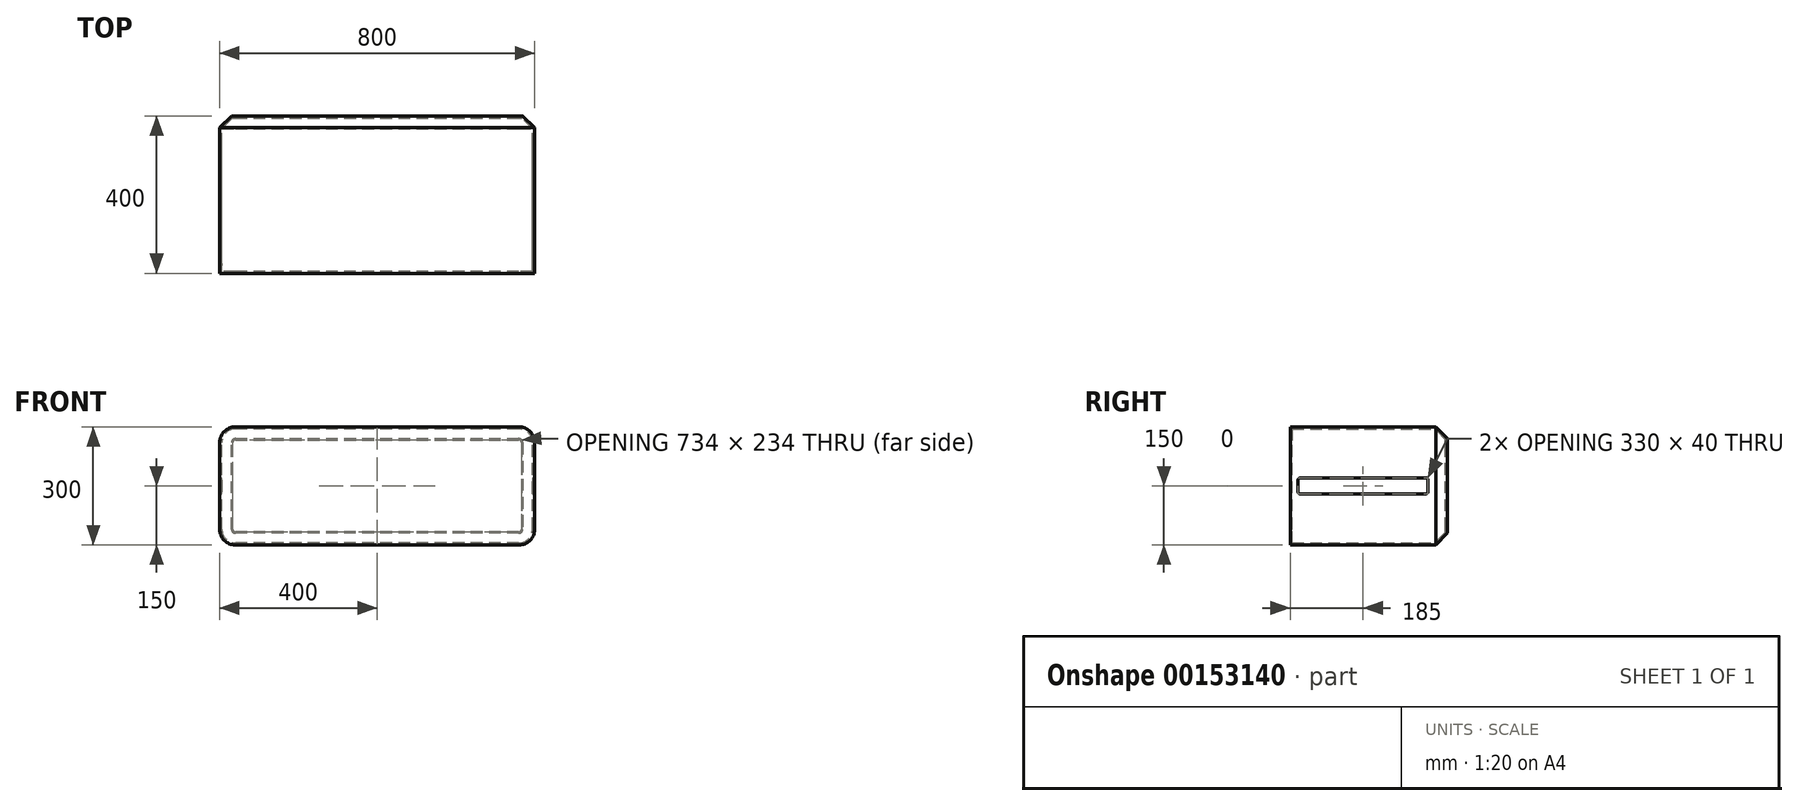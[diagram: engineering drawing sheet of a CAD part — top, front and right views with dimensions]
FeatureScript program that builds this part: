
annotation { "Feature Type Name" : "Feature", "Feature Type Description" : "" }
export const myFeature = defineFeature(function(context is Context, id is Id, definition is map)
    precondition{}
    {
        {
            var Q0;
            Q0=qCreatedBy(makeId("Front.planeOp"),FACE);
            var sketch = newSketch(context, id + "F0", { "sketchPlane" : qUnion([Q0])});
            skLineSegment(sketch, "E0.bottom", {"start": v(400, -150) * mm, "end": v(-400, -150) * mm});
            skLineSegment(sketch, "E0.top", {"start": v(400, 150) * mm, "end": v(-400, 150) * mm});
            skLineSegment(sketch, "E0.left", {"start": v(400, -150) * mm, "end": v(400, 150) * mm});
            skLineSegment(sketch, "E0.right", {"start": v(-400, -150) * mm, "end": v(-400, 150) * mm});
            skPoint(sketch, "E0.middle", {"position": v(0, 0) * mm});
            skSolve(sketch);
        }
        {
            var Q0;
            Q0=makeQuery(id+"F0.imprint","IMPRINT",FACE,{"disambiguationData":[TD([[makeQuery(id+"F0.imprint","IMPRINT",EDGE,{"derivedFrom":sQuery(id+"F0.wireOp",EDGE,"E0.bottom")}),-1.0]])]});
            extrude(context, id + "F1", {"entities" : qUnion([Q0]), "depth" : 400 * mm});
        }
        {
            var Q0;
            Q0=makeQuery(id+"F1.opExtrude","SWEPT_EDGE",EDGE,{"disambiguationData":[OSD([sQuery(id+"F0.wireOp",EDGE,"E0.top"),sQuery(id+"F0.wireOp",EDGE,"E0.left")])]});
            var Q1;
            Q1=makeQuery(id+"F1.opExtrude","SWEPT_EDGE",EDGE,{"disambiguationData":[OSD([sQuery(id+"F0.wireOp",EDGE,"E0.top"),sQuery(id+"F0.wireOp",EDGE,"E0.right")])]});
            var Q2;
            Q2=makeQuery(id+"F1.opExtrude","SWEPT_EDGE",EDGE,{"disambiguationData":[OSD([sQuery(id+"F0.wireOp",EDGE,"E0.bottom"),sQuery(id+"F0.wireOp",EDGE,"E0.left")])]});
            var Q3;
            Q3=makeQuery(id+"F1.opExtrude","SWEPT_EDGE",EDGE,{"disambiguationData":[OSD([sQuery(id+"F0.wireOp",EDGE,"E0.bottom"),sQuery(id+"F0.wireOp",EDGE,"E0.right")])]});
            fillet(context, id + "F2", {"entities" : qUnion([Q0, Q1, Q2, Q3]), "radius" : 40 * mm, "tangentPropagation" : true, "allowEdgeOverflow" : false});
        }
        {
            var Q0;
            Q0=makeQuery(id+"F1.opExtrude","CAP_EDGE",EDGE,{"disambiguationData":[OSD([sQuery(id+"F0.wireOp",EDGE,"E0.top")])],"isStart":true});
            chamfer(context, id + "F3", {"entities" : qUnion([Q0]), "width" : 30 * mm, "tangentPropagation" : true});
        }
        {
            var Q0;
            Q0=makeQuery(id+"F1.opExtrude","CAP_FACE",FACE,{"disambiguationData":[OSD([sQuery(id+"F0.wireOp",EDGE,"E0.bottom"),sQuery(id+"F0.wireOp",EDGE,"E0.top"),sQuery(id+"F0.wireOp",EDGE,"E0.left"),sQuery(id+"F0.wireOp",EDGE,"E0.right")])],"isStart":true});
            var sketch = newSketch(context, id + "F4", { "sketchPlane" : qUnion([Q0])});
            skArc(sketch, "E1.0", {"start": v(367, 110) * mm, "mid": v(364.95, 114.95) * mm, "end": v(360, 117) * mm});
            skLineSegment(sketch, "E1.1", {"start": v(367, -110) * mm, "end": v(367, 110) * mm});
            skLineSegment(sketch, "E1.2", {"start": v(360, 117) * mm, "end": v(-360, 117) * mm});
            skArc(sketch, "E1.3", {"start": v(360, -117) * mm, "mid": v(364.95, -114.95) * mm, "end": v(367, -110) * mm});
            skArc(sketch, "E1.4", {"start": v(-360, 117) * mm, "mid": v(-364.95, 114.95) * mm, "end": v(-367, 110) * mm});
            skLineSegment(sketch, "E1.5", {"start": v(-367, 110) * mm, "end": v(-367, -110) * mm});
            skArc(sketch, "E1.6", {"start": v(-367, -110) * mm, "mid": v(-364.95, -114.95) * mm, "end": v(-360, -117) * mm});
            skLineSegment(sketch, "E1.7", {"start": v(-360, -117) * mm, "end": v(360, -117) * mm});
            skSolve(sketch);
        }
        {
            var Q0;
            Q0=makeQuery(id+"F4.imprint","IMPRINT",FACE,{"disambiguationData":[TD([[makeQuery(id+"F4.imprint","IMPRINT",EDGE,{"derivedFrom":sQuery(id+"F4.wireOp",EDGE,"E1.0")}),1.0]])]});
            extrude(context, id + "F5", {"entities" : qUnion([Q0]), "operationType" : NewBodyOperationType.REMOVE, "oppositeDirection" : true, "depth" : 5 * mm});
        }
        {
            var Q0;
            Q0=makeQuery(id+"F5.boolean.opBoolean","COPY",FACE,{"derivedFrom":makeQuery(id+"F5.opExtrude","CAP_FACE",FACE,{"disambiguationData":[OSD([sQuery(id+"F4.wireOp",EDGE,"E1.0"),sQuery(id+"F4.wireOp",EDGE,"E1.1"),sQuery(id+"F4.wireOp",EDGE,"E1.2"),sQuery(id+"F4.wireOp",EDGE,"E1.3"),sQuery(id+"F4.wireOp",EDGE,"E1.4"),sQuery(id+"F4.wireOp",EDGE,"E1.5"),sQuery(id+"F4.wireOp",EDGE,"E1.6"),sQuery(id+"F4.wireOp",EDGE,"E1.7")])],"isStart":false})});
            shell(context, id + "F6", {"entities" : qUnion([Q0]), "thickness" : 5 * mm});
        }
        {
            var Q0;
            Q0=makeQuery(id+"F1.opExtrude","SWEPT_FACE",FACE,{"disambiguationData":[OSD([sQuery(id+"F0.wireOp",EDGE,"E0.left")])]});
            var sketch = newSketch(context, id + "F7", { "sketchPlane" : qUnion([Q0])});
            skLineSegment(sketch, "E2.bottom", {"start": v(-55, -20) * mm, "end": v(-375, -20) * mm});
            skLineSegment(sketch, "E2.top", {"start": v(-55, 20) * mm, "end": v(-375, 20) * mm});
            skLineSegment(sketch, "E2.left", {"start": v(-50, -15) * mm, "end": v(-50, 15) * mm});
            skLineSegment(sketch, "E2.right", {"start": v(-380, -15) * mm, "end": v(-380, 15) * mm});
            skPoint(sketch, "E2.middle", {"position": v(-215, 0) * mm});
            skPoint(sketch, "E2.middle.positionSnap0", {"position": v(-30, 0) * mm});
            skPoint(sketch, "E2.centerSnap0", {"position": v(-30, 0) * mm});
            skPoint(sketch, "E3.visualSharp", {"position": v(-50, 20) * mm});
            skArc(sketch, "E3.filletArc", {"start": v(-50, 15) * mm, "mid": v(-51.46, 18.54) * mm, "end": v(-55, 20) * mm});
            skPoint(sketch, "E4.visualSharp", {"position": v(-50, -20) * mm});
            skArc(sketch, "E4.filletArc", {"start": v(-55, -20) * mm, "mid": v(-51.46, -18.54) * mm, "end": v(-50, -15) * mm});
            skPoint(sketch, "E5.visualSharp", {"position": v(-380, -20) * mm});
            skArc(sketch, "E5.filletArc", {"start": v(-380, -15) * mm, "mid": v(-378.54, -18.54) * mm, "end": v(-375, -20) * mm});
            skPoint(sketch, "E6.visualSharp", {"position": v(-380, 20) * mm});
            skArc(sketch, "E6.filletArc", {"start": v(-375, 20) * mm, "mid": v(-378.54, 18.54) * mm, "end": v(-380, 15) * mm});
            skSolve(sketch);
        }
        {
            var Q0;
            Q0=makeQuery(id+"F7.imprint","IMPRINT",FACE,{"disambiguationData":[TD([[makeQuery(id+"F7.imprint","IMPRINT",EDGE,{"derivedFrom":sQuery(id+"F7.wireOp",EDGE,"E2.bottom")}),-1.0]])]});
            extrude(context, id + "F8", {"entities" : qUnion([Q0]), "operationType" : NewBodyOperationType.REMOVE, "endBound" : BoundingType.THROUGH_ALL, "oppositeDirection" : true, "depth" : 25 * mm});
        }
    });
